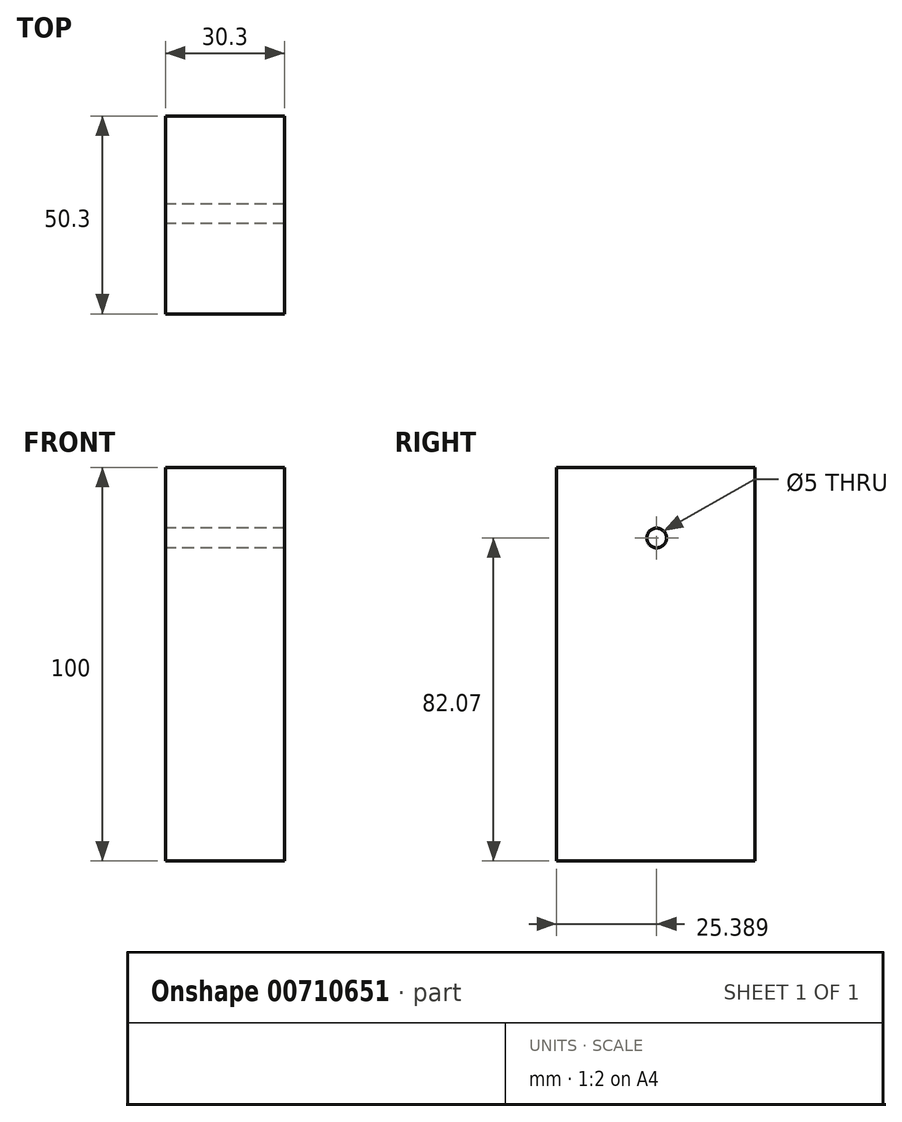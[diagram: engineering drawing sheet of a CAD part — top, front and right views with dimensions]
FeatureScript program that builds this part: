
annotation { "Feature Type Name" : "Feature", "Feature Type Description" : "" }
export const myFeature = defineFeature(function(context is Context, id is Id, definition is map)
    precondition{}
    {
        {
            var Q0;
            Q0=qCreatedBy(makeId("Top.planeOp"),FACE);
            var sketch = newSketch(context, id + "F0", { "sketchPlane" : qUnion([Q0])});
            skLineSegment(sketch, "E0.bottom", {"start": v(50.19, 44.82) * mm, "end": v(19.9, 44.82) * mm});
            skLineSegment(sketch, "E0.top", {"start": v(50.19, -5.48) * mm, "end": v(19.9, -5.48) * mm});
            skLineSegment(sketch, "E0.left", {"start": v(50.19, 44.82) * mm, "end": v(50.19, -5.48) * mm});
            skLineSegment(sketch, "E0.right", {"start": v(19.9, 44.82) * mm, "end": v(19.9, -5.48) * mm});
            skSolve(sketch);
        }
        {
            var Q0;
            Q0=makeQuery(id+"F0.imprint","IMPRINT",FACE,{"disambiguationData":[TD([[makeQuery(id+"F0.imprint","IMPRINT",EDGE,{"derivedFrom":sQuery(id+"F0.wireOp",EDGE,"E0.bottom")}),1.0]])]});
            extrude(context, id + "F1", {"entities" : qUnion([Q0]), "depth" : 100 * mm, "offsetDistance" : 25 * mm});
        }
        {
            var Q0;
            Q0=makeQuery(id+"F1.opExtrude","SWEPT_FACE",FACE,{"disambiguationData":[OSD([sQuery(id+"F0.wireOp",EDGE,"E0.right")])]});
            var sketch = newSketch(context, id + "F2", { "sketchPlane" : qUnion([Q0])});
            skCircle(sketch, "E1", {"center": v(-19.9, 82.07) * mm, "radius": 12.97 * mm});
            skSolve(sketch);
        }
        {
            var Q0;
            Q0=sQuery(id+"F2.wireOp",VERTEX,"E1.center");
            var Q1;
            Q1=makeQuery(id+"F1.opExtrude","SWEPT_BODY",BODY,{"disambiguationData":[OSD([sQuery(id+"F0.wireOp",EDGE,"E0.bottom"),sQuery(id+"F0.wireOp",EDGE,"E0.top"),sQuery(id+"F0.wireOp",EDGE,"E0.left"),sQuery(id+"F0.wireOp",EDGE,"E0.right")])]});
            hole(context, id + "F3", {"style" : HoleStyle.SIMPLE, "endStyle" : HoleEndStyle.THROUGH, "holeDiameter" : 5 * mm, "majorDiameter" : 5 * mm, "isTappedThrough" : true, "tappedDepth" : 12 * mm, "tapClearance" : 3, "locations" : qUnion([Q0]), "scope" : qUnion([Q1])});
        }
    });
